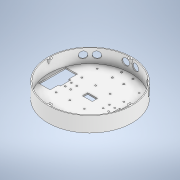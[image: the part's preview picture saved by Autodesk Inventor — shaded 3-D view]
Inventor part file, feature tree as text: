
AUTODESK INVENTOR PART (.ipt)
format: ipt  version: 2021 (Build 250183000, 183)  size: 663,040 bytes
history: native  units: mm
features: extrude x12, other x9, sketch x8, plane x8, reference x6, pattern_circular x2, hole x2, mirror x1, loft x1, projected_geometry x1
ambient origin geometry x8: Origin, YZ Plane, XZ Plane, XY Plane, X Axis, Y Axis, Z Axis, Center Point
bodies: Volumenkörper1 (feature_tree)
feature tree (50):
  other  "00_Mastersketch.ipt"
  extrude  "Extrusion1"  Depth=3.6mm TaperAngle=0.0deg
  extrude  "Extrusion2"  Depth=36.0mm
  extrude  "Extrusion3"  Depth=45.0mm
  extrude  "Extrusion5"  Depth=4.0mm
  pattern_circular  "Runde Anordnung1"  Count=64 Angle=360.0deg
  extrude  "Extrusion4"  TaperAngle=0.0deg  [1 undecoded]
  extrude  "Extrusion8"  TaperAngle=0.0deg  [1 undecoded]
  mirror  "Spiegeln1"
  sketch  "Skizze3"  dims[d3=45.0mm d4=0.0mm d5=36.0mm]
  plane  "Arbeitsebene1"
  sketch  "Skizze4"  dims[d6=0.0mm d7=45.0mm]
  loft  "Erhebung2"
  hole  "Bohrung2"  [1 undecoded]
  pattern_circular  "Runde Anordnung2"  [2 undecoded]
  plane  "Arbeitsebene2"
  extrude  "Extrusion6"  Depth=10.0mm TaperAngle=0.0deg
  extrude  "Extrusion7"  Depth=10.0mm TaperAngle=0.0deg
  extrude  "Extrusion9"  TaperAngle=0.0deg  [1 undecoded]
  plane  "Arbeitsebene_Ultra_1_Extrusion"
  plane  "Arbeitsebene_Ultra_2_Extrusion"
  extrude  "Extrusion11"  Depth=2.0mm
  extrude  "Extrusion12"  TaperAngle=0.0deg  [1 undecoded]
  hole  "Bohrung3"  [1 undecoded]
  extrude  "Extrusion10"  TaperAngle=0.0deg  [1 undecoded]
  other  "01_caseBottom"
  sketch  "Skizze2"  dims[d0=10.0mm d1=3.6mm d2=0.0mm]
  other  "3D-Skizze2"
  other  "Arbeitsachse1"
  sketch  "Skizze5"  dims[d8=0.0mm d9=4.0mm]
  reference  "Referenz1"
  reference  "Referenz2"
  sketch  "Skizze6"  dims[d10=6.0mm]
  plane  "Arbeitsebene_Ultra_1_Angle"
  plane  "Arbeitsebene_Ultra_1_Extrusion_Helper"
  plane  "Arbeitsebene_Ultra_2_"
  plane  "Arbeitsebene_Ultra_2_Extrusion_Helper"
  sketch  "Skizze7"  dims[d11=0.0mm d12=0.0mm d13=640.0mm d14=360.0deg]
  projected_geometry  "Projizierte Kontur1"
  reference  "Referenz3"
  reference  "Referenz4"
  sketch  "Skizze8"  dims[d17=-15.0mm d31=0.0mm d32=90.0deg]
  reference  "Referenz5"
  reference  "Referenz6"
  sketch  "Skizze9"  dims[d33=0.0mm d34=90.0deg d35=0.0mm d36=90.0deg d37=3.35mm d38=6.0mm d39=4.0mm d40=2.0mm d41=90.0deg d42=5.0mm d43=0.0mm d44=40.0mm d45=360.0deg d47=1.0mm d48=1.0mm d49=10.0mm d50=0.0mm d51=10.0mm d52=0.0mm d53=0.0mm d54=0.0mm d55=2.0mm d56=0.0mm d57=0.0mm d58=1.0mm d60=0.0mm d61=0.0mm d62=45.0deg d63=90.0deg d64=-7.853982mm d65=90.0deg d66=1.0mm d67=10.0mm d68=0.0mm d69=1.0mm d70=10.0mm d71=0.0mm d74=4.2mm d75=0.2mm d76=110.0mm d77=40.0mm d78=36.0mm d79=4.0mm d80=6.0mm d81=4.0mm d82=2.0mm d83=90.0deg d84=5.0mm d85=0.0mm]
  other  "<userpath>\Desktop\Bachelorarbeit\CAD\00_RobotAssembly.iam"
  other  "00_RobotAssembly.iam"
  other  "HC-SR04:1"
  other  "HC-SR04:3"
  other  "HC-SR04:2"
note: 9 required parameter values undecoded (feature->parameter linkage not recoverable at this tier; creation-order binding heuristic only, values carry confidence <= 0.55)
